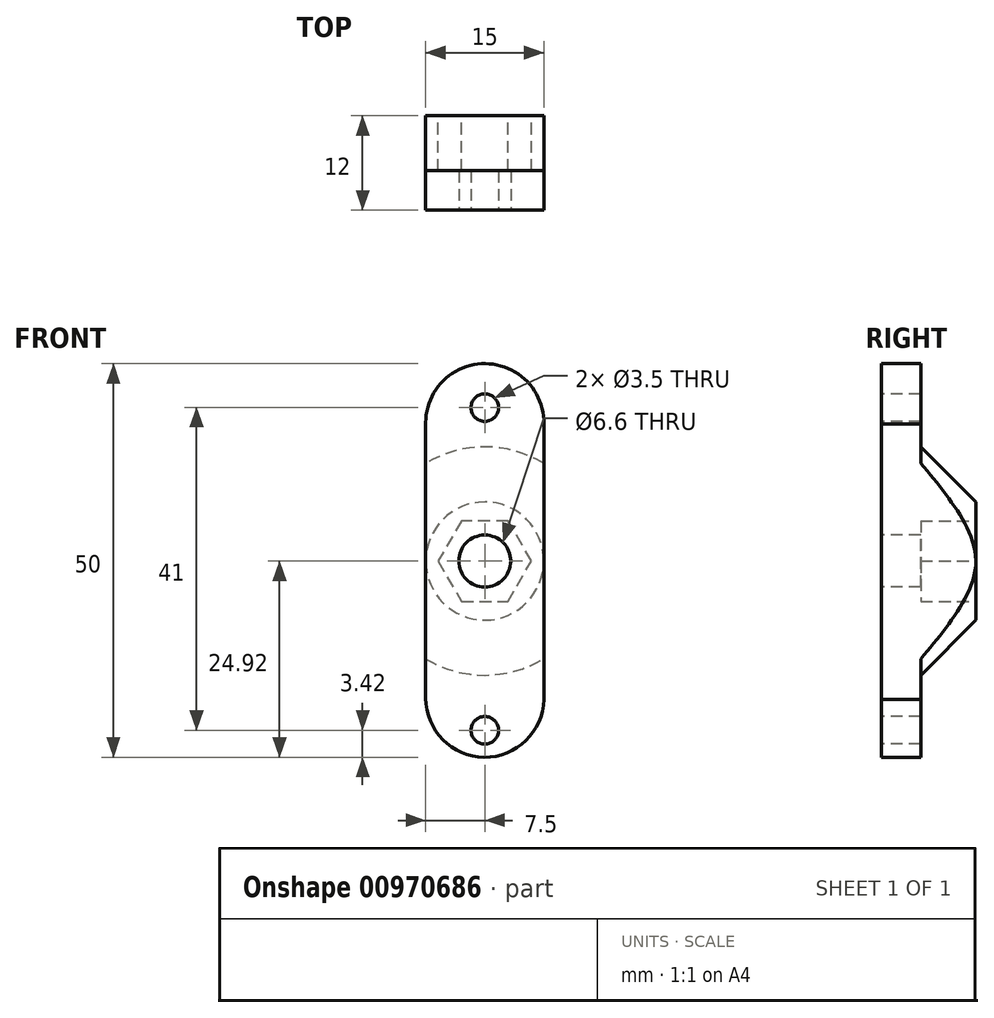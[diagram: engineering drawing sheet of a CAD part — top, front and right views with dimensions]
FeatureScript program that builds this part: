
annotation { "Feature Type Name" : "Feature", "Feature Type Description" : "" }
export const myFeature = defineFeature(function(context is Context, id is Id, definition is map)
    precondition{}
    {
        {
            var Q0;
            Q0=qCreatedBy(makeId("Front.planeOp"),FACE);
            var sketch = newSketch(context, id + "F0", { "sketchPlane" : qUnion([Q0])});
            skLineSegment(sketch, "E0.left", {"start": v(7.5, -17.58) * mm, "end": v(7.5, 17.42) * mm});
            skLineSegment(sketch, "E0.right", {"start": v(-7.5, -17.42) * mm, "end": v(-7.5, 17.58) * mm});
            skPoint(sketch, "E0.middle", {"position": v(0, 0) * mm});
            skArc(sketch, "E1", {"start": v(-7.5, 17.58) * mm, "mid": v(0.08, 25.08) * mm, "end": v(7.5, 17.42) * mm});
            skArc(sketch, "E2", {"start": v(-7.5, -17.42) * mm, "mid": v(-0.08, -24.92) * mm, "end": v(7.5, -17.58) * mm});
            skSolve(sketch);
        }
        {
            var Q0;
            Q0 = qSketchRegion(id + "F0", true);
            extrude(context, id + "F1", {"entities" : qUnion([Q0]), "depth" : 5 * mm, "offsetDistance" : 25 * mm});
        }
        {
            var Q0;
            Q0=makeQuery(id+"F1.opExtrude","CAP_FACE",FACE,{"disambiguationData":[OSD([sQuery(id+"F0.wireOp",EDGE,"E0.left"),sQuery(id+"F0.wireOp",EDGE,"E0.right"),sQuery(id+"F0.wireOp",EDGE,"E1"),sQuery(id+"F0.wireOp",EDGE,"E2")])],"isStart":true});
            var sketch = newSketch(context, id + "F2", { "sketchPlane" : qUnion([Q0])});
            skCircle(sketch, "E3", {"center": v(0, 0) * mm, "radius": 7.5 * mm});
            skSolve(sketch);
        }
        {
            var Q0;
            Q0 = qSketchRegion(id + "F2", true);
            extrude(context, id + "F3", {"entities" : qUnion([Q0]), "operationType" : NewBodyOperationType.ADD, "depth" : 7 * mm, "offsetDistance" : 25 * mm});
        }
        {
            var Q0;
            Q0=makeQuery(id+"F1.opExtrude","CAP_FACE",FACE,{"disambiguationData":[OSD([sQuery(id+"F0.wireOp",EDGE,"E0.left"),sQuery(id+"F0.wireOp",EDGE,"E0.right"),sQuery(id+"F0.wireOp",EDGE,"E1"),sQuery(id+"F0.wireOp",EDGE,"E2")])],"isStart":false});
            var sketch = newSketch(context, id + "F4", { "sketchPlane" : qUnion([Q0])});
            skPoint(sketch, "E4", {"position": v(0, 0) * mm});
            skSolve(sketch);
        }
        {
            var Q0;
            Q0=sQuery(id+"F4.wireOp",VERTEX,"E4");
            var Q1;
            Q1=makeQuery(id+"F1.opExtrude","SWEPT_BODY",BODY,{"disambiguationData":[OSD([sQuery(id+"F0.wireOp",EDGE,"E0.left"),sQuery(id+"F0.wireOp",EDGE,"E0.right"),sQuery(id+"F0.wireOp",EDGE,"E1"),sQuery(id+"F0.wireOp",EDGE,"E2")])]});
            hole(context, id + "F5", {"style" : HoleStyle.SIMPLE, "endStyle" : HoleEndStyle.THROUGH, "standardTappedOrClearance" : lookupTablePath({ "standard" : "ISO", "fit" : "Normal", "size" : "M6", "type" : "Clearance" }), "standardBlindInLast" : lookupTablePath({ "fit" : "Normal", "standard" : "ISO", "engagement" : "75%", "pitch" : "1 mm", "size" : "M6", "type" : "Clearance & tapped" }), "holeDiameter" : 6.6 * mm, "majorDiameter" : 5 * mm, "isTappedThrough" : true, "tappedDepth" : 12 * mm, "tapClearance" : 3, "locations" : qUnion([Q0]), "scope" : qUnion([Q1])});
        }
        {
            var Q0;
            Q0=makeQuery(id+"F3.opExtrude","CAP_FACE",FACE,{"disambiguationData":[OSD([sQuery(id+"F2.wireOp",EDGE,"E3")])],"isStart":false});
            var sketch = newSketch(context, id + "F6", { "sketchPlane" : qUnion([Q0])});
            skCircle(sketch, "E5.cCircle", {"center": v(0, 0) * mm, "radius": 5.12 * mm, "construction": true});
            skLineSegment(sketch, "E5.0", {"start": v(5.92, 0) * mm, "end": v(2.96, -5.13) * mm});
            skLineSegment(sketch, "E5.1", {"start": v(2.96, -5.12) * mm, "end": v(-2.96, -5.12) * mm});
            skLineSegment(sketch, "E5.2", {"start": v(-2.96, -5.12) * mm, "end": v(-5.92, 0) * mm});
            skLineSegment(sketch, "E5.3", {"start": v(-5.92, 0) * mm, "end": v(-2.96, 5.12) * mm});
            skLineSegment(sketch, "E5.4", {"start": v(-2.96, 5.12) * mm, "end": v(2.96, 5.12) * mm});
            skLineSegment(sketch, "E5.5", {"start": v(2.96, 5.13) * mm, "end": v(5.92, 0) * mm});
            skPoint(sketch, "E5.0.midPoint", {"position": v(4.44, -2.56) * mm});
            skSolve(sketch);
        }
        {
            var Q0;
            Q0 = qSketchRegion(id + "F6", true);
            var Q1;
            {var subQ0=sQuery(id+"F0.wireOp",EDGE,"E1");var subQ1=sQuery(id+"F0.wireOp",EDGE,"E0.right");var subQ2=sQuery(id+"F0.wireOp",EDGE,"E0.left");var subQ3=makeQuery(id+"F1.opExtrude","CAP_FACE",FACE,{"disambiguationData":[OSD([subQ2,subQ1,subQ0,sQuery(id+"F0.wireOp",EDGE,"E2")])],"isStart":true});Q1=makeQuery(id+"F3.boolean.opBoolean","SPLIT",FACE,{"disambiguationData":[TD([makeQuery(id+"F1.opExtrude","SWEPT_FACE",FACE,{"disambiguationData":[OSD([subQ0])]})])],"derivedFrom":subQ3});}
            extrude(context, id + "F7", {"entities" : qUnion([Q0]), "operationType" : NewBodyOperationType.REMOVE, "endBound" : BoundingType.UP_TO_SURFACE, "oppositeDirection" : true, "depth" : 25 * mm, "endBoundEntityFace" : qUnion([Q1]), "offsetDistance" : 25 * mm});
        }
        {
            var Q0;
            Q0=makeQuery(id+"F1.opExtrude","CAP_FACE",FACE,{"disambiguationData":[OSD([sQuery(id+"F0.wireOp",EDGE,"E0.left"),sQuery(id+"F0.wireOp",EDGE,"E0.right"),sQuery(id+"F0.wireOp",EDGE,"E1"),sQuery(id+"F0.wireOp",EDGE,"E2")])],"isStart":false});
            var sketch = newSketch(context, id + "F8", { "sketchPlane" : qUnion([Q0])});
            skPoint(sketch, "E6", {"position": v(0, 19.5) * mm});
            skPoint(sketch, "E7", {"position": v(0, -21.5) * mm});
            skSolve(sketch);
        }
        {
            var Q0;
            Q0=makeQuery(id+"F3.boolean.opBoolean","SPLIT",EDGE,{"disambiguationData":[OD(0.0)],"derivedFrom":makeQuery(id+"F3.opExtrude","CAP_EDGE",EDGE,{"disambiguationData":[OSD([sQuery(id+"F2.wireOp",EDGE,"E3")])],"isStart":true})});
            var Q1;
            Q1=makeQuery(id+"F3.boolean.opBoolean","SPLIT",EDGE,{"disambiguationData":[OD(1.0)],"derivedFrom":makeQuery(id+"F3.opExtrude","CAP_EDGE",EDGE,{"disambiguationData":[OSD([sQuery(id+"F2.wireOp",EDGE,"E3")])],"isStart":true})});
            chamfer(context, id + "F9", {"entities" : qUnion([Q0, Q1]), "width" : 7 * mm, "tangentPropagation" : true});
        }
        {
            var Q0;
            Q0=sQuery(id+"F8.wireOp",VERTEX,"E6");
            var Q1;
            Q1=sQuery(id+"F8.wireOp",VERTEX,"E7");
            var Q2;
            Q2=makeQuery(id+"F1.opExtrude","SWEPT_BODY",BODY,{"disambiguationData":[OSD([sQuery(id+"F0.wireOp",EDGE,"E0.left"),sQuery(id+"F0.wireOp",EDGE,"E0.right"),sQuery(id+"F0.wireOp",EDGE,"E1"),sQuery(id+"F0.wireOp",EDGE,"E2")])]});
            hole(context, id + "F10", {"style" : HoleStyle.SIMPLE, "endStyle" : HoleEndStyle.THROUGH, "holeDiameter" : 3.5 * mm, "majorDiameter" : 5 * mm, "isTappedThrough" : true, "tappedDepth" : 12 * mm, "tapClearance" : 3, "locations" : qUnion([Q0, Q1]), "scope" : qUnion([Q2])});
        }
    });
